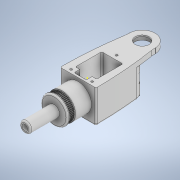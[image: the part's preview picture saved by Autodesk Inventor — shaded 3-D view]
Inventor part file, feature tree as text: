
AUTODESK INVENTOR PART (.ipt)
format: ipt  version: 2021 (Build 250183000, 183)  size: 2,230,784 bytes
history: native  units: mm
features: sketch x36, extrude x35, fillet x11, other x1
ambient origin geometry x8: Origin, YZ Plane, XZ Plane, XY Plane, X Axis, Y Axis, Z Axis, Center Point
bodies: Body1 (feature_tree)
feature tree (83):
  other  "Bryła1"
  extrude  "Wyciągnięcie proste1"  Depth=5.7mm TaperAngle=0.0deg
  extrude  "Wyciągnięcie proste2"  Depth=18.95mm
  sketch  "Szkic7"
  extrude  "Wyciągnięcie proste3"  Depth=1.25mm TaperAngle=0.0deg
  extrude  "Wyciągnięcie proste4"  Depth=34.0mm
  extrude  "Wyciągnięcie proste7"  Depth=26.0mm TaperAngle=0.0deg
  extrude  "Wyciągnięcie proste8"  TaperAngle=0.0deg  [1 undecoded]
  fillet  "Zaokrąglenie1"  Radius=22.5mm
  extrude  "Wyciągnięcie proste9"  Depth=22.1mm
  sketch  "Szkic20"
  extrude  "Wyciągnięcie proste10"  Depth=22.1mm
  sketch  "Szkic22"
  extrude  "Wyciągnięcie proste11"  Depth=3.0mm TaperAngle=0.0deg
  sketch  "Szkic26"
  extrude  "Wyciągnięcie proste13"  Depth=1.0mm
  fillet  "Zaokrąglenie2"  Radius=1.0mm
  fillet  "Zaokrąglenie3"  Radius=30.5mm
  sketch  "Szkic33"
  extrude  "Wyciągnięcie proste14"  Depth=10.0mm TaperAngle=0.0deg
  fillet  "Zaokrąglenie4"  Radius=2.5mm
  fillet  "Zaokrąglenie5"  Radius=29.0mm
  extrude  "Wyciągnięcie proste17"  Depth=2.0mm
  extrude  "Wyciągnięcie proste19"  Depth=2.0mm
  extrude  "Wyciągnięcie proste20"  Depth=2.0mm
  extrude  "Wyciągnięcie proste21"  Depth=2.0mm
  extrude  "Wyciągnięcie proste22"  Depth=32.95mm TaperAngle=0.0deg
  extrude  "Wyciągnięcie proste24"  Depth=16.475mm TaperAngle=0.0deg
  fillet  "Zaokrąglenie8"  Radius=19.5mm
  fillet  "Zaokrąglenie9"  Radius=9.75mm
  fillet  "Zaokrąglenie10"  Radius=9.75mm
  sketch  "Szkic58"
  extrude  "Wyciągnięcie proste27"  Depth=6.95mm TaperAngle=0.0deg
  sketch  "Szkic65"
  extrude  "Wyciągnięcie proste28"  Depth=550.0mm
  extrude  "Wyciągnięcie proste29"  Depth=15.0mm
  extrude  "Wyciągnięcie proste30"  Depth=6.95mm TaperAngle=0.0deg
  extrude  "Wyciągnięcie proste31"  Depth=550.0mm
  extrude  "Wyciągnięcie proste32"  Depth=15.0mm
  extrude  "Wyciągnięcie proste33"  Depth=2.0mm TaperAngle=0.0deg
  extrude  "Wyciągnięcie proste34"  Depth=10.0mm TaperAngle=0.0deg
  fillet  "Zaokrąglenie12"  Radius=37.0mm
  sketch  "Szkic78"
  extrude  "Wyciągnięcie proste37"  Depth=22.0mm TaperAngle=0.0deg
  extrude  "Wyciągnięcie proste38"  Depth=8.0mm TaperAngle=0.0deg
  fillet  "Zaokrąglenie13"  Radius=3.0mm
  extrude  "Wyciągnięcie proste40"  Depth=15.0mm TaperAngle=0.0deg
  extrude  "Wyciągnięcie proste41"  Depth=1.0mm
  extrude  "Wyciągnięcie proste42"  Depth=2.0mm
  extrude  "Wyciągnięcie proste44"  Depth=2.0mm
  extrude  "Wyciągnięcie proste45"  Depth=1.9mm
  extrude  "Wyciągnięcie proste48"  Depth=1.9mm
  extrude  "Wyciągnięcie proste49"  Depth=6.5mm
  extrude  "Wyciągnięcie proste51"  Depth=1.9mm
  fillet  "Zaokrąglenie15"  Radius=2.0mm
  sketch  "Szkic1"
  sketch  "Szkic2"
  sketch  "Szkic13"
  sketch  "Szkic15"
  sketch  "Szkic19"
  sketch  "Szkic23"
  sketch  "Szkic41"
  sketch  "Szkic42"
  sketch  "Szkic44"
  sketch  "Szkic45"
  sketch  "Szkic47"
  sketch  "Szkic51"
  sketch  "Szkic64"
  sketch  "Szkic67"
  sketch  "Szkic68"
  sketch  "Szkic69"
  sketch  "Szkic70"
  sketch  "Szkic71"
  sketch  "Szkic74"
  sketch  "Szkic81"
  sketch  "Szkic92"
  sketch  "Szkic93"
  sketch  "Szkic95"
  sketch  "Szkic99"
  sketch  "Szkic106"
  sketch  "Szkic109"
  sketch  "Szkic110"
  sketch  "Szkic119"
note: 1 required parameter value undecoded (feature->parameter linkage not recoverable at this tier; creation-order binding heuristic only, values carry confidence <= 0.55)
